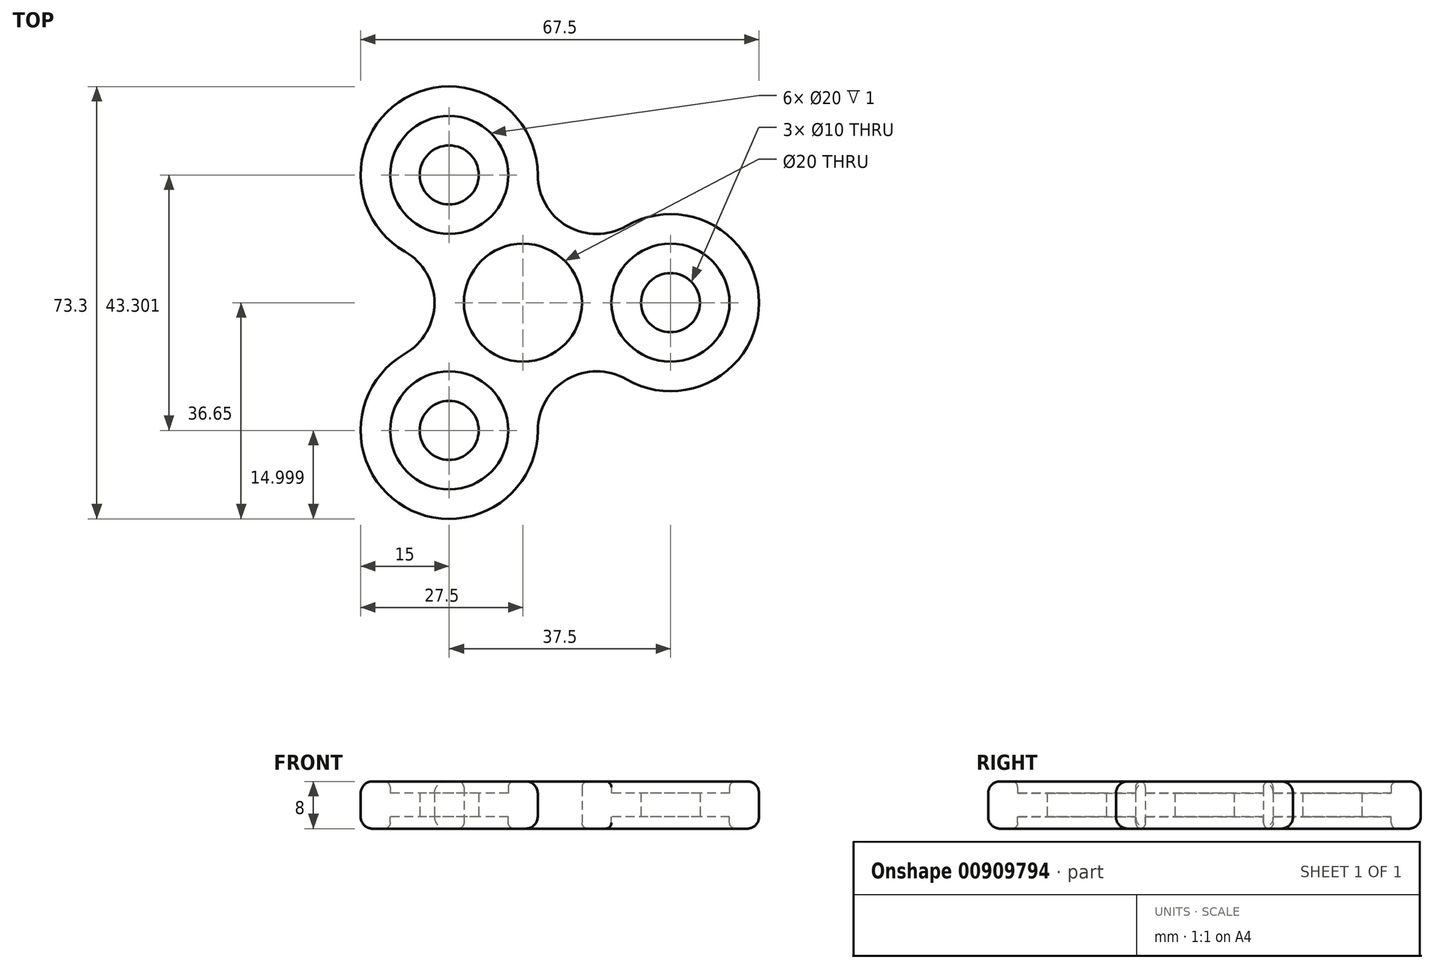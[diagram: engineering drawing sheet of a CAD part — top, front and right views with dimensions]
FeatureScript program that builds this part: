
annotation { "Feature Type Name" : "Feature", "Feature Type Description" : "" }
export const myFeature = defineFeature(function(context is Context, id is Id, definition is map)
    precondition{}
    {
        {
            var Q0;
            Q0=qCreatedBy(makeId("Top.planeOp"),FACE);
            var sketch = newSketch(context, id + "F0", { "sketchPlane" : qUnion([Q0])});
            skCircle(sketch, "E0", {"center": v(0, 0) * mm, "radius": 10 * mm});
            skCircle(sketch, "E1", {"center": v(25, 0) * mm, "radius": 10 * mm});
            skCircle(sketch, "E2", {"center": v(0, 0) * mm, "radius": 5 * mm});
            skCircle(sketch, "E3", {"center": v(25, 0) * mm, "radius": 5 * mm});
            skArc(sketch, "E4", {"start": v(17.5, -13) * mm, "mid": v(40, 0) * mm, "end": v(17.5, 13) * mm});
            skLineSegment(sketch, "E5", {"start": v(7.5, 13) * mm, "end": v(7.5, 13) * mm});
            skPoint(sketch, "E6", {"position": v(12.5, 8.3) * mm});
            skPoint(sketch, "E7", {"position": v(12.5, -8.3) * mm});
            skArc(sketch, "E8.1.0", {"start": v(2.5, 21.65) * mm, "mid": v(-20, 34.64) * mm, "end": v(-20, 8.66) * mm});
            skCircle(sketch, "E8.1.1", {"center": v(-12.5, 21.65) * mm, "radius": 10 * mm});
            skPoint(sketch, "E8.1.2", {"position": v(-13.43, 6.68) * mm});
            skCircle(sketch, "E8.1.3", {"center": v(-12.5, 21.65) * mm, "radius": 5 * mm});
            skPoint(sketch, "E8.1.4", {"position": v(0.93, 14.97) * mm});
            skArc(sketch, "E8.2.0", {"start": v(-20, -8.66) * mm, "mid": v(-20, -34.64) * mm, "end": v(2.5, -21.65) * mm});
            skCircle(sketch, "E8.2.1", {"center": v(-12.5, -21.65) * mm, "radius": 10 * mm});
            skPoint(sketch, "E8.2.2", {"position": v(0.93, -14.97) * mm});
            skCircle(sketch, "E8.2.3", {"center": v(-12.5, -21.65) * mm, "radius": 5 * mm});
            skPoint(sketch, "E8.2.4", {"position": v(-13.43, -6.68) * mm});
            skLineSegment(sketch, "E9.trimOffspring", {"start": v(-15, 0) * mm, "end": v(-15, 0) * mm});
            skLineSegment(sketch, "E10.trimOffspring", {"start": v(7.5, -13) * mm, "end": v(7.5, -13) * mm});
            skArc(sketch, "E11.filletArc", {"start": v(2.5, 21.65) * mm, "mid": v(3.84, 16.65) * mm, "end": v(7.5, 13) * mm});
            skArc(sketch, "E12.filletArc", {"start": v(7.5, 13) * mm, "mid": v(12.5, 11.65) * mm, "end": v(17.5, 13) * mm});
            skArc(sketch, "E13.filletArc", {"start": v(17.5, -13) * mm, "mid": v(12.5, -11.65) * mm, "end": v(7.5, -13) * mm});
            skArc(sketch, "E14.filletArc", {"start": v(7.5, -13) * mm, "mid": v(3.84, -16.65) * mm, "end": v(2.5, -21.65) * mm});
            skArc(sketch, "E15.filletArc", {"start": v(-20, -8.66) * mm, "mid": v(-16.34, -5) * mm, "end": v(-15, 0) * mm});
            skArc(sketch, "E16.filletArc", {"start": v(-15, 0) * mm, "mid": v(-16.34, 5) * mm, "end": v(-20, 8.66) * mm});
            skSolve(sketch);
        }
        {
            var Q0;
            Q0=qSketchRegion(id+"F0",true);
            extrude(context, id + "F1", {"entities" : qUnion([Q0]), "depth" : 4 * mm, "offsetDistance" : 25 * mm});
        }
        {
            var Q0;
            Q0=makeQuery(id+"F0.imprint","IMPRINT",FACE,{"disambiguationData":[TD([[makeQuery(id+"F0.imprint","IMPRINT",EDGE,{"derivedFrom":sQuery(id+"F0.wireOp",EDGE,"E8.1.1")}),1.0]])]});
            var Q1;
            Q1=makeQuery(id+"F0.imprint","IMPRINT",FACE,{"disambiguationData":[TD([[makeQuery(id+"F0.imprint","IMPRINT",EDGE,{"derivedFrom":sQuery(id+"F0.wireOp",EDGE,"E1")}),1.0]])]});
            var Q2;
            Q2=makeQuery(id+"F0.imprint","IMPRINT",FACE,{"disambiguationData":[TD([[makeQuery(id+"F0.imprint","IMPRINT",EDGE,{"derivedFrom":sQuery(id+"F0.wireOp",EDGE,"E8.2.1")}),1.0]])]});
            extrude(context, id + "F2", {"entities" : qUnion([Q0, Q1, Q2]), "operationType" : NewBodyOperationType.ADD, "depth" : 2 * mm, "offsetDistance" : 25 * mm});
        }
        {
            var Q0;
            Q0=makeQuery(id+"F1.opExtrude","CAP_EDGE",EDGE,{"disambiguationData":[OSD([sQuery(id+"F0.wireOp",EDGE,"E8.1.1")])],"isStart":false});
            var Q1;
            Q1=makeQuery(id+"F1.opExtrude","CAP_EDGE",EDGE,{"disambiguationData":[OSD([sQuery(id+"F0.wireOp",EDGE,"E0")])],"isStart":false});
            var Q2;
            Q2=makeQuery(id+"F1.opExtrude","CAP_EDGE",EDGE,{"disambiguationData":[OSD([sQuery(id+"F0.wireOp",EDGE,"E1")])],"isStart":false});
            var Q3;
            Q3=makeQuery(id+"F1.opExtrude","CAP_EDGE",EDGE,{"disambiguationData":[OSD([sQuery(id+"F0.wireOp",EDGE,"E8.2.1")])],"isStart":false});
            fillet(context, id + "F3", {"entities" : qUnion([Q0, Q1, Q2, Q3]), "radius" : 1 * mm, "tangentPropagation" : true, "allowEdgeOverflow" : false});
        }
        {
            var Q0;
            Q0=makeQuery(id+"F1.opExtrude","CAP_EDGE",EDGE,{"disambiguationData":[OSD([sQuery(id+"F0.wireOp",EDGE,"E11.filletArc"),sQuery(id+"F0.wireOp",EDGE,"E12.filletArc")])],"isStart":false});
            var Q1;
            Q1=makeQuery(id+"F1.opExtrude","CAP_EDGE",EDGE,{"disambiguationData":[OSD([sQuery(id+"F0.wireOp",EDGE,"E8.1.0")])],"isStart":false});
            var Q2;
            Q2=makeQuery(id+"F1.opExtrude","CAP_EDGE",EDGE,{"disambiguationData":[OSD([sQuery(id+"F0.wireOp",EDGE,"E15.filletArc"),sQuery(id+"F0.wireOp",EDGE,"E16.filletArc")])],"isStart":false});
            var Q3;
            Q3=makeQuery(id+"F1.opExtrude","CAP_EDGE",EDGE,{"disambiguationData":[OSD([sQuery(id+"F0.wireOp",EDGE,"E8.2.0")])],"isStart":false});
            var Q4;
            Q4=makeQuery(id+"F1.opExtrude","CAP_EDGE",EDGE,{"disambiguationData":[OSD([sQuery(id+"F0.wireOp",EDGE,"E13.filletArc"),sQuery(id+"F0.wireOp",EDGE,"E14.filletArc")])],"isStart":false});
            var Q5;
            Q5=makeQuery(id+"F1.opExtrude","CAP_EDGE",EDGE,{"disambiguationData":[OSD([sQuery(id+"F0.wireOp",EDGE,"E4")])],"isStart":false});
            fillet(context, id + "F4", {"entities" : qUnion([Q0, Q1, Q2, Q3, Q4, Q5]), "radius" : 2 * mm, "tangentPropagation" : true, "allowEdgeOverflow" : false});
        }
        {
            var Q0;
            Q0=makeQuery(id+"F1.opExtrude","SWEPT_BODY",BODY,{"disambiguationData":[OSD([sQuery(id+"F0.wireOp",EDGE,"E0"),sQuery(id+"F0.wireOp",EDGE,"E1"),sQuery(id+"F0.wireOp",EDGE,"E4"),sQuery(id+"F0.wireOp",EDGE,"E8.1.0"),sQuery(id+"F0.wireOp",EDGE,"E8.1.1"),sQuery(id+"F0.wireOp",EDGE,"E8.2.0"),sQuery(id+"F0.wireOp",EDGE,"E8.2.1"),sQuery(id+"F0.wireOp",EDGE,"E11.filletArc"),sQuery(id+"F0.wireOp",EDGE,"E12.filletArc"),sQuery(id+"F0.wireOp",EDGE,"E13.filletArc"),sQuery(id+"F0.wireOp",EDGE,"E14.filletArc"),sQuery(id+"F0.wireOp",EDGE,"E15.filletArc"),sQuery(id+"F0.wireOp",EDGE,"E16.filletArc")])]});
            var Q1;
            Q1=qCreatedBy(makeId("Top.planeOp"),FACE);
            mirror(context, id + "F5", {"operationType" : NewBodyOperationType.ADD, "entities" : qUnion([Q0]), "mirrorPlane" : qUnion([Q1])});
        }
    });
